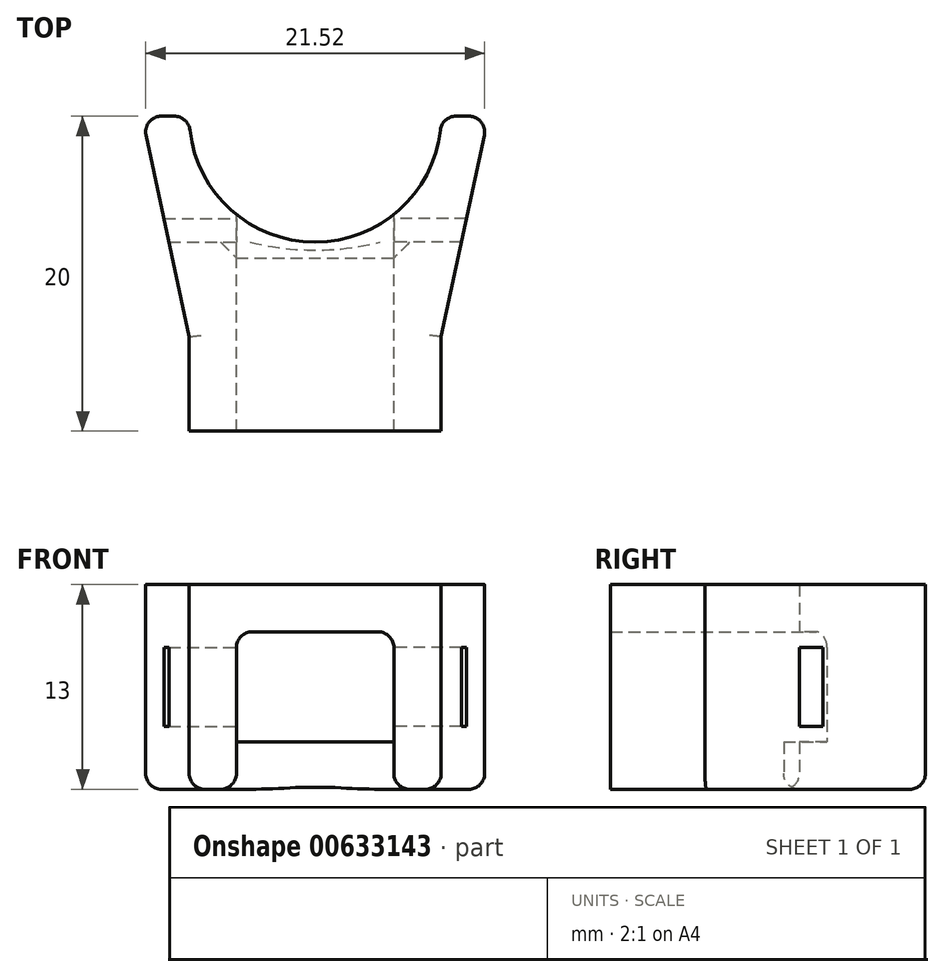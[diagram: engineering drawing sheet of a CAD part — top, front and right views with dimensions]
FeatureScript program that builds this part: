
annotation { "Feature Type Name" : "Feature", "Feature Type Description" : "" }
export const myFeature = defineFeature(function(context is Context, id is Id, definition is map)
    precondition{}
    {
        {
            var Q0;
            Q0=qCreatedBy(makeId("Front.planeOp"),FACE);
            var sketch = newSketch(context, id + "F0", { "sketchPlane" : qUnion([Q0])});
            skLineSegment(sketch, "E0", {"start": v(0, 0) * mm, "end": v(0, 10) * mm});
            skLineSegment(sketch, "E1", {"start": v(0, 10) * mm, "end": v(5, 10) * mm});
            skLineSegment(sketch, "E2", {"start": v(5, 10) * mm, "end": v(5, 0) * mm});
            skLineSegment(sketch, "E3", {"start": v(5, 0) * mm, "end": v(8, 0) * mm});
            skLineSegment(sketch, "E4", {"start": v(8, 0) * mm, "end": v(8, 13) * mm});
            skLineSegment(sketch, "E5", {"start": v(8, 13) * mm, "end": v(0, 13) * mm});
            skLineSegment(sketch, "E6", {"start": v(0, 13) * mm, "end": v(0, 10) * mm});
            skSolve(sketch);
        }
        {
            var Q0;
            Q0 = qSketchRegion(id + "F0", true);
            extrude(context, id + "F1", {"entities" : qUnion([Q0]), "endBound" : BoundingType.SYMMETRIC, "depth" : 12 * mm, "offsetDistance" : 25 * mm});
        }
        {
            var Q0;
            Q0=qCreatedBy(makeId("Top.planeOp"),FACE);
            var sketch = newSketch(context, id + "F2", { "sketchPlane" : qUnion([Q0])});
            skLineSegment(sketch, "E7", {"start": v(0, 0) * mm, "end": v(8, 0) * mm});
            skLineSegment(sketch, "E8", {"start": v(8, 0) * mm, "end": v(8, 14) * mm, "construction": true});
            skLineSegment(sketch, "E9", {"start": v(8, 14) * mm, "end": v(11, 14) * mm});
            skLineSegment(sketch, "E10", {"start": v(11, 14) * mm, "end": v(8, 0) * mm});
            skArc(sketch, "E11", {"start": v(0, 6) * mm, "mid": v(5.66, 8.34) * mm, "end": v(8, 14) * mm});
            skLineSegment(sketch, "E12", {"start": v(0, 6) * mm, "end": v(0, 0) * mm});
            skSolve(sketch);
        }
        {
            var Q0;
            Q0=makeQuery(id+"F2.imprint","IMPRINT",FACE,{"disambiguationData":[TD([[makeQuery(id+"F2.imprint","IMPRINT",EDGE,{"derivedFrom":sQuery(id+"F2.wireOp",EDGE,"E7")}),1.0]])]});
            extrude(context, id + "F3", {"entities" : qUnion([Q0]), "depth" : 13 * mm, "offsetDistance" : 25 * mm});
        }
        {
            var Q0;
            Q0=makeQuery(id+"F3.opExtrude","SWEPT_BODY",BODY,{"disambiguationData":[OSD([sQuery(id+"F2.wireOp",EDGE,"E7"),sQuery(id+"F2.wireOp",EDGE,"E9"),sQuery(id+"F2.wireOp",EDGE,"E10"),sQuery(id+"F2.wireOp",EDGE,"E11"),sQuery(id+"F2.wireOp",EDGE,"E12")])]});
            transform(context, id + "F4", {"entities" : qUnion([Q0]), "transformType" : TransformType.TRANSLATION_3D, "dx" : 0 * mm, "dy" : 0 * mm, "dz" : 0 * mm, "makeCopy" : false});
        }
        {
            var Q0;
            Q0=qCreatedBy(makeId("Front.planeOp"),FACE);
            var sketch = newSketch(context, id + "F5", { "sketchPlane" : qUnion([Q0])});
            skLineSegment(sketch, "E13.top", {"start": v(0, 10) * mm, "end": v(5, 10) * mm});
            skLineSegment(sketch, "E13.left", {"start": v(0, 0) * mm, "end": v(0, 10) * mm});
            skLineSegment(sketch, "E13.right", {"start": v(5, 0) * mm, "end": v(5, 10) * mm});
            skLineSegment(sketch, "E14", {"start": v(0, 0) * mm, "end": v(0, 3) * mm});
            skLineSegment(sketch, "E15", {"start": v(0, 3) * mm, "end": v(5, 3) * mm});
            skSolve(sketch);
        }
        {
            var Q0;
            Q0 = qSketchRegion(id + "F5", true);
            extrude(context, id + "F6", {"entities" : qUnion([Q0]), "endBound" : BoundingType.SYMMETRIC, "depth" : 25 * mm, "offsetDistance" : 25 * mm});
        }
        {
            var Q0;
            Q0=makeQuery(id+"F6.opExtrude","SWEPT_BODY",BODY,{"disambiguationData":[OSD([sQuery(id+"F5.wireOp",EDGE,"E13.bottom"),sQuery(id+"F5.wireOp",EDGE,"E13.top"),sQuery(id+"F5.wireOp",EDGE,"E13.left"),sQuery(id+"F5.wireOp",EDGE,"E13.right")])]});
            var Q1;
            Q1=makeQuery(id+"F3.opExtrude","SWEPT_BODY",BODY,{"disambiguationData":[OSD([sQuery(id+"F2.wireOp",EDGE,"E7"),sQuery(id+"F2.wireOp",EDGE,"E9"),sQuery(id+"F2.wireOp",EDGE,"E10"),sQuery(id+"F2.wireOp",EDGE,"E11"),sQuery(id+"F2.wireOp",EDGE,"E12")])]});
            booleanBodies(context, id + "F7", {"operationType" : BooleanOperationType.SUBTRACTION, "tools" : qUnion([Q0]), "targets" : qUnion([Q1])});
        }
        {
            var Q0;
            Q0=qCreatedBy(makeId("Right.planeOp"),FACE);
            var sketch = newSketch(context, id + "F8", { "sketchPlane" : qUnion([Q0])});
            skLineSegment(sketch, "E16", {"start": v(0, 0) * mm, "end": v(0, 9) * mm});
            skLineSegment(sketch, "E17", {"start": v(0, 9) * mm, "end": v(7.5, 9) * mm});
            skLineSegment(sketch, "E18", {"start": v(7.5, 9) * mm, "end": v(7.5, 4) * mm});
            skLineSegment(sketch, "E19", {"start": v(7.5, 4) * mm, "end": v(6, 4) * mm});
            skLineSegment(sketch, "E20", {"start": v(6, 4) * mm, "end": v(6, 9) * mm});
            skSolve(sketch);
        }
        {
            var Q0;
            {var subQ0=sQuery(id+"F8.wireOp",EDGE,"E18");Q0=makeQuery(id+"F8.imprint","IMPRINT",FACE,{"disambiguationData":[TD([[makeQuery(id+"F8.imprint","IMPRINT",EDGE,{"derivedFrom":subQ0}),-1.0]])]});}
            extrude(context, id + "F9", {"entities" : qUnion([Q0]), "depth" : 25 * mm, "offsetDistance" : 25 * mm});
        }
        {
            var Q0;
            Q0=makeQuery(id+"F9.opExtrude","SWEPT_BODY",BODY,{"disambiguationData":[OSD([sQuery(id+"F8.wireOp",EDGE,"E17"),sQuery(id+"F8.wireOp",EDGE,"E18"),sQuery(id+"F8.wireOp",EDGE,"E19"),sQuery(id+"F8.wireOp",EDGE,"E20")])]});
            var Q1;
            Q1=makeQuery(id+"F3.opExtrude","SWEPT_BODY",BODY,{"disambiguationData":[OSD([sQuery(id+"F2.wireOp",EDGE,"E7"),sQuery(id+"F2.wireOp",EDGE,"E9"),sQuery(id+"F2.wireOp",EDGE,"E10"),sQuery(id+"F2.wireOp",EDGE,"E11"),sQuery(id+"F2.wireOp",EDGE,"E12")])]});
            booleanBodies(context, id + "F10", {"operationType" : BooleanOperationType.SUBTRACTION, "tools" : qUnion([Q0]), "targets" : qUnion([Q1])});
        }
        {
            var Q0;
            Q0=qCreatedBy(makeId("Top.planeOp"),FACE);
            var sketch = newSketch(context, id + "F11", { "sketchPlane" : qUnion([Q0])});
            skLineSegment(sketch, "E21", {"start": v(0, 0) * mm, "end": v(5, 0) * mm});
            skLineSegment(sketch, "E22", {"start": v(5, 0) * mm, "end": v(5, 5) * mm});
            skLineSegment(sketch, "E23", {"start": v(5, 5) * mm, "end": v(0, 5) * mm});
            skLineSegment(sketch, "E24", {"start": v(0, 5) * mm, "end": v(0, 0) * mm});
            skSolve(sketch);
        }
        {
            var Q0;
            Q0 = qSketchRegion(id + "F11", true);
            extrude(context, id + "F12", {"entities" : qUnion([Q0]), "endBound" : BoundingType.SYMMETRIC, "depth" : 8 * mm, "offsetDistance" : 25 * mm});
        }
        {
            var Q0;
            Q0=makeQuery(id+"F12.opExtrude","SWEPT_BODY",BODY,{"disambiguationData":[OSD([sQuery(id+"F11.wireOp",EDGE,"E21"),sQuery(id+"F11.wireOp",EDGE,"E22"),sQuery(id+"F11.wireOp",EDGE,"E23"),sQuery(id+"F11.wireOp",EDGE,"E24")])]});
            var Q1;
            Q1=makeQuery(id+"F3.opExtrude","SWEPT_BODY",BODY,{"disambiguationData":[OSD([sQuery(id+"F2.wireOp",EDGE,"E7"),sQuery(id+"F2.wireOp",EDGE,"E9"),sQuery(id+"F2.wireOp",EDGE,"E10"),sQuery(id+"F2.wireOp",EDGE,"E11"),sQuery(id+"F2.wireOp",EDGE,"E12")])]});
            booleanBodies(context, id + "F13", {"operationType" : BooleanOperationType.SUBTRACTION, "tools" : qUnion([Q0]), "targets" : qUnion([Q1])});
        }
        {
            var Q0;
            Q0=makeQuery(id+"F1.opExtrude","SWEPT_BODY",BODY,{"disambiguationData":[OSD([sQuery(id+"F0.wireOp",EDGE,"E1"),sQuery(id+"F0.wireOp",EDGE,"E2"),sQuery(id+"F0.wireOp",EDGE,"E3"),sQuery(id+"F0.wireOp",EDGE,"E4"),sQuery(id+"F0.wireOp",EDGE,"E5"),sQuery(id+"F0.wireOp",EDGE,"E6")])]});
            var Q1;
            Q1=makeQuery(id+"F3.opExtrude","SWEPT_BODY",BODY,{"disambiguationData":[OSD([sQuery(id+"F2.wireOp",EDGE,"E7"),sQuery(id+"F2.wireOp",EDGE,"E9"),sQuery(id+"F2.wireOp",EDGE,"E10"),sQuery(id+"F2.wireOp",EDGE,"E11"),sQuery(id+"F2.wireOp",EDGE,"E12")])]});
            booleanBodies(context, id + "F14", {"operationType" : BooleanOperationType.UNION, "tools" : qUnion([Q0, Q1])});
        }
        {
            var Q0;
            Q0=makeQuery(id+"F3.opExtrude","SWEPT_EDGE",EDGE,{"disambiguationData":[OSD([sQuery(id+"F2.wireOp",EDGE,"E9"),sQuery(id+"F2.wireOp",EDGE,"E10")])]});
            var Q1;
            Q1=makeQuery(id+"F3.opExtrude","SWEPT_EDGE",EDGE,{"disambiguationData":[OSD([sQuery(id+"F2.wireOp",EDGE,"E9"),sQuery(id+"F2.wireOp",EDGE,"E11")])]});
            var Q2;
            Q2=makeQuery(id+"F7.opBoolean","COPY",EDGE,{"derivedFrom":makeQuery(id+"F6.opExtrude","SWEPT_EDGE",EDGE,{"disambiguationData":[OSD([sQuery(id+"F5.wireOp",EDGE,"E13.right"),sQuery(id+"F5.wireOp",EDGE,"E15")])]})});
            var Q3;
            Q3=makeQuery(id+"F14.opBoolean","MERGE",EDGE,{"derivedFrom":[makeQuery(id+"F1.opExtrude","SWEPT_EDGE",EDGE,{"disambiguationData":[OSD([sQuery(id+"F0.wireOp",EDGE,"E1"),sQuery(id+"F0.wireOp",EDGE,"E2")])]}),makeQuery(id+"F7.opBoolean","COPY",EDGE,{"derivedFrom":makeQuery(id+"F6.opExtrude","SWEPT_EDGE",EDGE,{"disambiguationData":[OSD([sQuery(id+"F5.wireOp",EDGE,"E13.top"),sQuery(id+"F5.wireOp",EDGE,"E13.right")])]})})]});
            var Q4;
            Q4=makeQuery(id+"F1.opExtrude","SWEPT_EDGE",EDGE,{"disambiguationData":[OSD([sQuery(id+"F0.wireOp",EDGE,"E2"),sQuery(id+"F0.wireOp",EDGE,"E3")])]});
            var Q5;
            Q5=makeQuery(id+"F13.opBoolean","INTERSECT",EDGE,{"derivedFrom":[makeQuery(id+"F3.opExtrude","CAP_FACE",FACE,{"disambiguationData":[OSD([sQuery(id+"F2.wireOp",EDGE,"E7"),sQuery(id+"F2.wireOp",EDGE,"E9"),sQuery(id+"F2.wireOp",EDGE,"E10"),sQuery(id+"F2.wireOp",EDGE,"E11"),sQuery(id+"F2.wireOp",EDGE,"E12")])],"isStart":true}),makeQuery(id+"F12.opExtrude","SWEPT_FACE",FACE,{"disambiguationData":[OSD([sQuery(id+"F11.wireOp",EDGE,"E23")])]})]});
            var Q6;
            Q6=makeQuery(id+"F3.opExtrude","CAP_EDGE",EDGE,{"disambiguationData":[OSD([sQuery(id+"F2.wireOp",EDGE,"E11")])],"isStart":true});
            var Q7;
            Q7=makeQuery(id+"F3.opExtrude","CAP_EDGE",EDGE,{"disambiguationData":[OSD([sQuery(id+"F2.wireOp",EDGE,"E10")])],"isStart":true});
            var Q8;
            Q8=makeQuery(id+"F1.opExtrude","SWEPT_EDGE",EDGE,{"disambiguationData":[OSD([sQuery(id+"F0.wireOp",EDGE,"E3"),sQuery(id+"F0.wireOp",EDGE,"E4")])]});
            var Q9;
            Q9=makeQuery(id+"F3.opExtrude","CAP_EDGE",EDGE,{"disambiguationData":[OSD([sQuery(id+"F2.wireOp",EDGE,"E9")])],"isStart":true});
            fillet(context, id + "F15", {"entities" : qUnion([Q0, Q1, Q2, Q3, Q4, Q5, Q6, Q7, Q8, Q9]), "radius" : 1 * mm, "tangentPropagation" : true, "allowEdgeOverflow" : false});
        }
        {
            var Q0;
            Q0=makeQuery(id+"F1.opExtrude","SWEPT_BODY",BODY,{"disambiguationData":[OSD([sQuery(id+"F0.wireOp",EDGE,"E1"),sQuery(id+"F0.wireOp",EDGE,"E2"),sQuery(id+"F0.wireOp",EDGE,"E3"),sQuery(id+"F0.wireOp",EDGE,"E4"),sQuery(id+"F0.wireOp",EDGE,"E5"),sQuery(id+"F0.wireOp",EDGE,"E6")])]});
            var Q1;
            Q1=qCreatedBy(makeId("Right.planeOp"),FACE);
            mirror(context, id + "F16", {"operationType" : NewBodyOperationType.ADD, "entities" : qUnion([Q0]), "mirrorPlane" : qUnion([Q1])});
        }
    });
